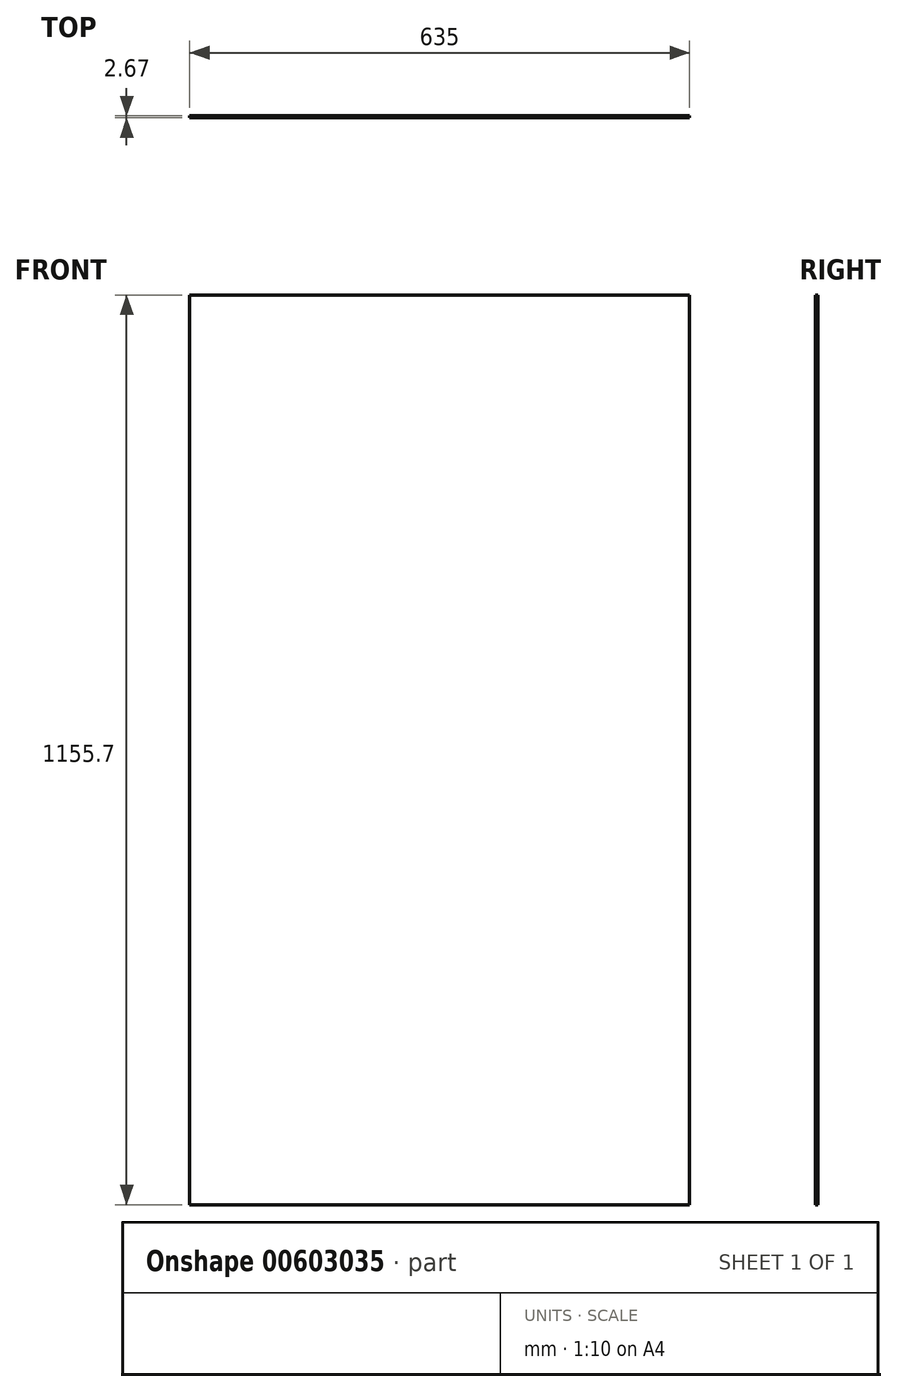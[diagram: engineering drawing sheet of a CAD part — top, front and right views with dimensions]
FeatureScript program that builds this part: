
annotation { "Feature Type Name" : "Feature", "Feature Type Description" : "" }
export const myFeature = defineFeature(function(context is Context, id is Id, definition is map)
    precondition{}
    {
        {
            var Q0;
            Q0=qCreatedBy(makeId("Front.planeOp"),FACE);
            var sketch = newSketch(context, id + "F0", { "sketchPlane" : qUnion([Q0])});
            skLineSegment(sketch, "E0.bottom", {"start": v(0, 0) * mm, "end": v(635, 0) * mm});
            skLineSegment(sketch, "E0.top", {"start": v(0, 1155.7) * mm, "end": v(635, 1155.7) * mm});
            skLineSegment(sketch, "E0.left", {"start": v(0, 0) * mm, "end": v(0, 1155.7) * mm});
            skLineSegment(sketch, "E0.right", {"start": v(635, 0) * mm, "end": v(635, 1155.7) * mm});
            skSolve(sketch);
        }
        {
            var Q0;
            Q0 = qSketchRegion(id + "F0", true);
            extrude(context, id + "F1", {"entities" : qUnion([Q0]), "depth" : 2.67 * mm, "offsetDistance" : 25.4 * mm});
        }
    });
